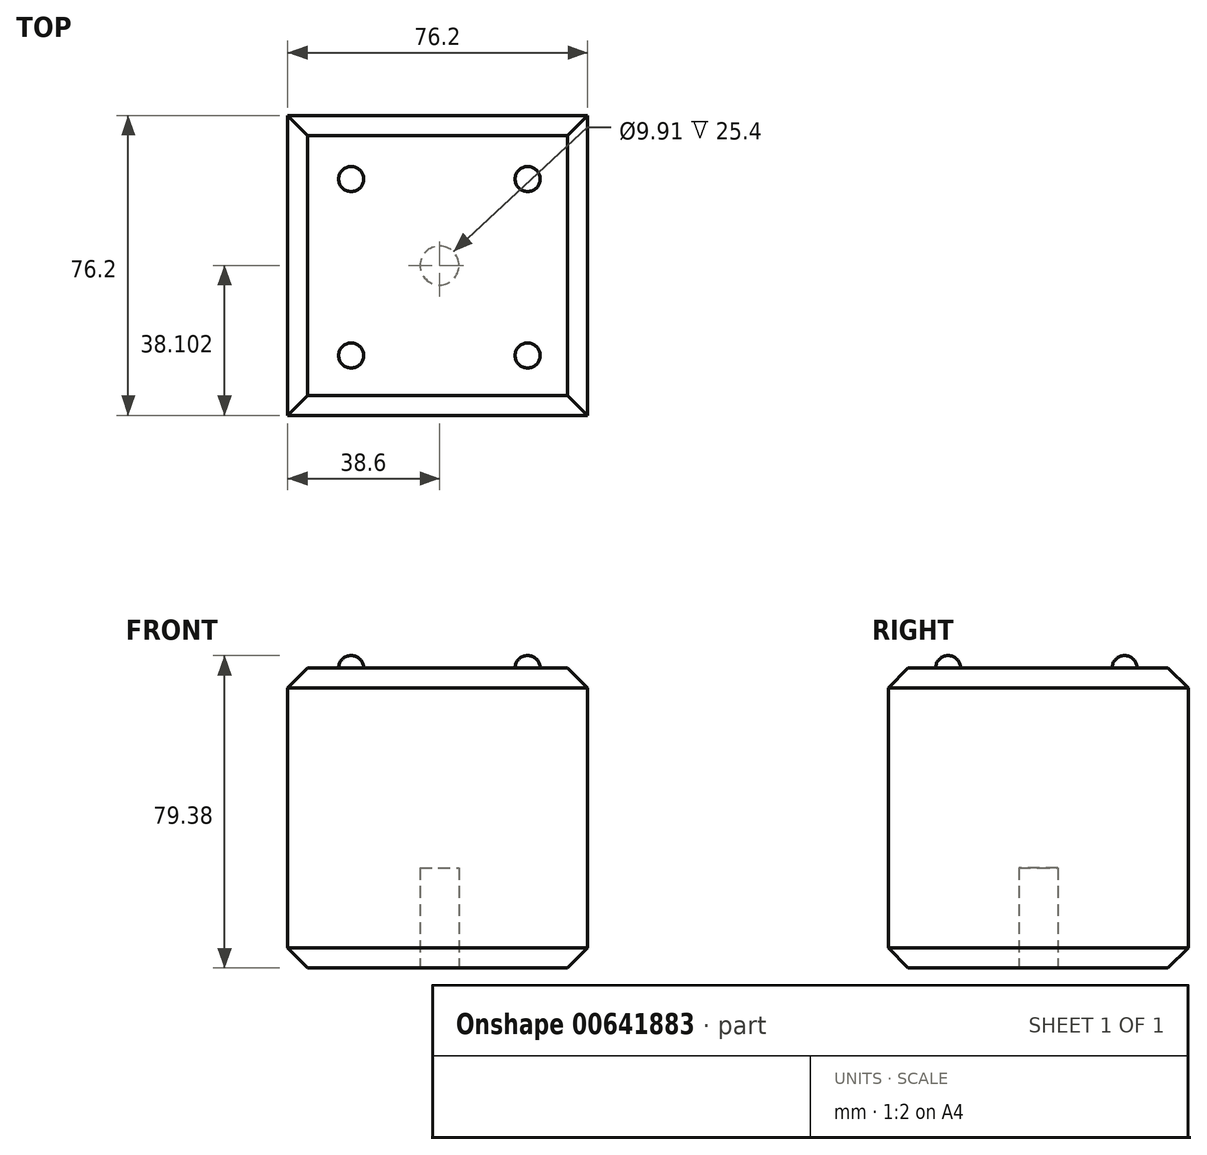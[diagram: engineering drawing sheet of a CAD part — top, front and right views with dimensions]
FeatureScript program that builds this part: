
annotation { "Feature Type Name" : "Feature", "Feature Type Description" : "" }
export const myFeature = defineFeature(function(context is Context, id is Id, definition is map)
    precondition{}
    {
        {
            var Q0;
            Q0=qCreatedBy(makeId("Top.planeOp"),FACE);
            var sketch = newSketch(context, id + "F0", { "sketchPlane" : qUnion([Q0])});
            skLineSegment(sketch, "E0.bottom", {"start": v(-38.6, -60.07) * mm, "end": v(37.6, -60.07) * mm});
            skLineSegment(sketch, "E0.top", {"start": v(-38.6, 16.13) * mm, "end": v(37.6, 16.13) * mm});
            skLineSegment(sketch, "E0.left", {"start": v(-38.6, -60.07) * mm, "end": v(-38.6, 16.13) * mm});
            skLineSegment(sketch, "E0.right", {"start": v(37.6, -60.07) * mm, "end": v(37.6, 16.13) * mm});
            skSolve(sketch);
        }
        {
            var Q0;
            Q0 = qSketchRegion(id + "F0", true);
            extrude(context, id + "F1", {"entities" : qUnion([Q0]), "depth" : 76.2 * mm, "offsetDistance" : 25.4 * mm});
        }
        {
            var Q0;
            Q0=makeQuery(id+"F1.opExtrude","CAP_EDGE",EDGE,{"disambiguationData":[OSD([sQuery(id+"F0.wireOp",EDGE,"E0.bottom")])],"isStart":false});
            var Q1;
            Q1=makeQuery(id+"F1.opExtrude","CAP_EDGE",EDGE,{"disambiguationData":[OSD([sQuery(id+"F0.wireOp",EDGE,"E0.right")])],"isStart":false});
            var Q2;
            Q2=makeQuery(id+"F1.opExtrude","CAP_EDGE",EDGE,{"disambiguationData":[OSD([sQuery(id+"F0.wireOp",EDGE,"E0.top")])],"isStart":false});
            var Q3;
            Q3=makeQuery(id+"F1.opExtrude","CAP_EDGE",EDGE,{"disambiguationData":[OSD([sQuery(id+"F0.wireOp",EDGE,"E0.left")])],"isStart":false});
            var Q4;
            Q4=makeQuery(id+"F1.opExtrude","CAP_EDGE",EDGE,{"disambiguationData":[OSD([sQuery(id+"F0.wireOp",EDGE,"E0.right")])],"isStart":true});
            var Q5;
            Q5=makeQuery(id+"F1.opExtrude","CAP_EDGE",EDGE,{"disambiguationData":[OSD([sQuery(id+"F0.wireOp",EDGE,"E0.bottom")])],"isStart":true});
            var Q6;
            Q6=makeQuery(id+"F1.opExtrude","CAP_EDGE",EDGE,{"disambiguationData":[OSD([sQuery(id+"F0.wireOp",EDGE,"E0.left")])],"isStart":true});
            var Q7;
            Q7=makeQuery(id+"F1.opExtrude","CAP_EDGE",EDGE,{"disambiguationData":[OSD([sQuery(id+"F0.wireOp",EDGE,"E0.top")])],"isStart":true});
            chamfer(context, id + "F2", {"entities" : qUnion([Q0, Q1, Q2, Q3, Q4, Q5, Q6, Q7]), "width" : 5.08 * mm, "tangentPropagation" : true});
        }
        {
            var Q0;
            Q0=makeQuery(id+"F1.opExtrude","CAP_FACE",FACE,{"disambiguationData":[OSD([sQuery(id+"F0.wireOp",EDGE,"E0.bottom"),sQuery(id+"F0.wireOp",EDGE,"E0.top"),sQuery(id+"F0.wireOp",EDGE,"E0.left"),sQuery(id+"F0.wireOp",EDGE,"E0.right")])],"isStart":true});
            var sketch = newSketch(context, id + "F3", { "sketchPlane" : qUnion([Q0])});
            skCircle(sketch, "E1", {"center": v(0, 21.97) * mm, "radius": 4.95 * mm});
            skPoint(sketch, "E1.centerSnap0", {"position": v(-0.5, 21.97) * mm});
            skSolve(sketch);
        }
        {
            var Q0;
            Q0 = qSketchRegion(id + "F3", true);
            extrude(context, id + "F4", {"entities" : qUnion([Q0]), "operationType" : NewBodyOperationType.REMOVE, "oppositeDirection" : true, "depth" : 25.4 * mm, "offsetDistance" : 25.4 * mm});
        }
        {
            var Q0;
            Q0=makeQuery(id+"F1.opExtrude","CAP_FACE",FACE,{"disambiguationData":[OSD([sQuery(id+"F0.wireOp",EDGE,"E0.bottom"),sQuery(id+"F0.wireOp",EDGE,"E0.top"),sQuery(id+"F0.wireOp",EDGE,"E0.left"),sQuery(id+"F0.wireOp",EDGE,"E0.right")])],"isStart":false});
            var sketch = newSketch(context, id + "F5", { "sketchPlane" : qUnion([Q0])});
            skCircle(sketch, "E2", {"center": v(-22.46, 0) * mm, "radius": 3.18 * mm});
            skCircle(sketch, "E3", {"center": v(22.36, 0) * mm, "radius": 3.18 * mm});
            skCircle(sketch, "E4", {"center": v(-22.46, -44.83) * mm, "radius": 3.18 * mm});
            skCircle(sketch, "E5", {"center": v(22.36, -44.83) * mm, "radius": 3.18 * mm});
            skSolve(sketch);
        }
        {
            var Q0;
            Q0 = qSketchRegion(id + "F5", true);
            extrude(context, id + "F6", {"entities" : qUnion([Q0]), "operationType" : NewBodyOperationType.ADD, "depth" : 3.17 * mm, "offsetDistance" : 25.4 * mm});
        }
        {
            var Q0;
            Q0=makeQuery(id+"F6.opExtrude","CAP_EDGE",EDGE,{"disambiguationData":[OSD([sQuery(id+"F5.wireOp",EDGE,"E4")])],"isStart":false});
            var Q1;
            Q1=makeQuery(id+"F6.opExtrude","CAP_EDGE",EDGE,{"disambiguationData":[OSD([sQuery(id+"F5.wireOp",EDGE,"E2")])],"isStart":false});
            var Q2;
            Q2=makeQuery(id+"F6.opExtrude","CAP_EDGE",EDGE,{"disambiguationData":[OSD([sQuery(id+"F5.wireOp",EDGE,"E3")])],"isStart":false});
            var Q3;
            Q3=makeQuery(id+"F6.opExtrude","CAP_EDGE",EDGE,{"disambiguationData":[OSD([sQuery(id+"F5.wireOp",EDGE,"E5")])],"isStart":false});
            fillet(context, id + "F7", {"entities" : qUnion([Q0, Q1, Q2, Q3]), "radius" : 3.17 * mm, "tangentPropagation" : true, "allowEdgeOverflow" : false});
        }
    });
